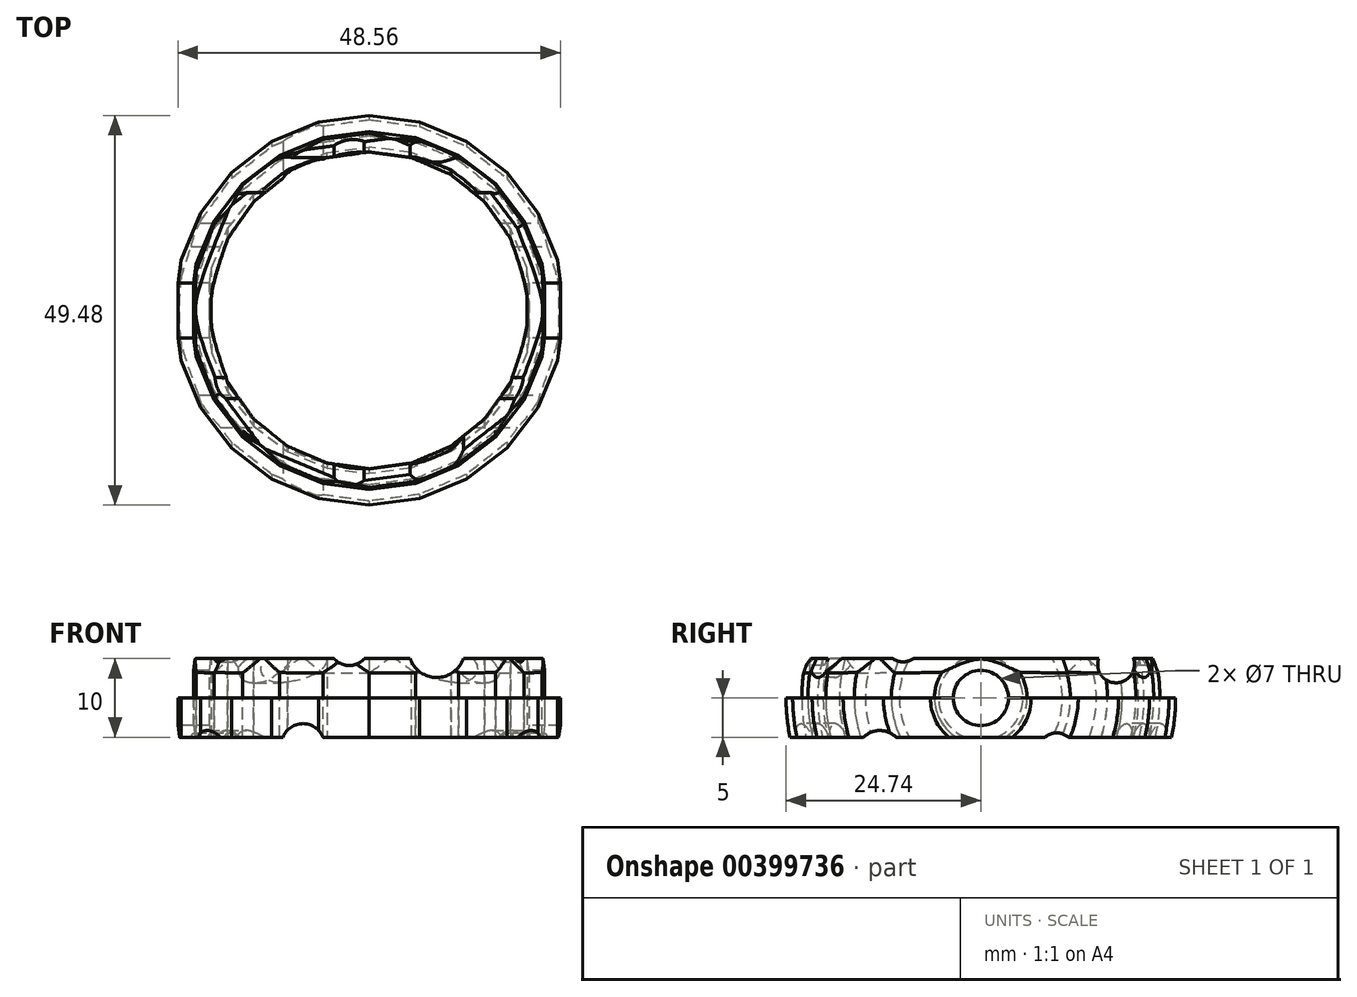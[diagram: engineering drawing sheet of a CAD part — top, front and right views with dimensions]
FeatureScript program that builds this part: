
annotation { "Feature Type Name" : "Feature", "Feature Type Description" : "" }
export const myFeature = defineFeature(function(context is Context, id is Id, definition is map)
    precondition{}
    {
        {
            var Q0;
            Q0=qCreatedBy(makeId("Top.planeOp"),FACE);
            var sketch = newSketch(context, id + "F0", { "sketchPlane" : qUnion([Q0])});
            skLineSegment(sketch, "E0", {"start": v(-24.74, 0) * mm, "end": v(24.74, 0) * mm});
            skLineSegment(sketch, "E1", {"start": v(-24.74, 0) * mm, "end": v(-22.74, 0) * mm});
            skLineSegment(sketch, "E2", {"start": v(24.74, 0) * mm, "end": v(22.74, 0) * mm});
            skLineSegment(sketch, "E3", {"start": v(0, 0) * mm, "end": v(-21.43, -12.37) * mm});
            skLineSegment(sketch, "E4", {"start": v(0, 0) * mm, "end": v(-23.9, -6.4) * mm});
            skLineSegment(sketch, "E5", {"start": v(-23.9, -6.4) * mm, "end": v(0, 0) * mm});
            skLineSegment(sketch, "E6", {"start": v(0, 0) * mm, "end": v(-17.5, -17.5) * mm});
            skLineSegment(sketch, "E7", {"start": v(-17.5, -17.5) * mm, "end": v(0, 0) * mm});
            skLineSegment(sketch, "E8", {"start": v(0, 0) * mm, "end": v(12.37, -21.43) * mm});
            skLineSegment(sketch, "E9", {"start": v(12.37, -21.43) * mm, "end": v(0, 0) * mm});
            skLineSegment(sketch, "E10", {"start": v(0, 0) * mm, "end": v(17.5, -17.5) * mm});
            skLineSegment(sketch, "E11", {"start": v(17.5, -17.5) * mm, "end": v(0, 0) * mm});
            skLineSegment(sketch, "E12", {"start": v(0, 0) * mm, "end": v(21.43, -12.37) * mm});
            skLineSegment(sketch, "E13", {"start": v(0, 0) * mm, "end": v(-12.37, -21.43) * mm});
            skLineSegment(sketch, "E14", {"start": v(-12.37, -21.43) * mm, "end": v(0, 0) * mm});
            skLineSegment(sketch, "E15", {"start": v(0, 0) * mm, "end": v(-6.4, -23.9) * mm});
            skLineSegment(sketch, "E16", {"start": v(0, 0) * mm, "end": v(6.4, -23.9) * mm});
            skLineSegment(sketch, "E17", {"start": v(0, 0) * mm, "end": v(23.9, -6.4) * mm});
            skLineSegment(sketch, "E18", {"start": v(0, 0) * mm, "end": v(0, -24.74) * mm});
            skSolve(sketch);
        }
        {
            var Q0;
            Q0=qCreatedBy(makeId("Top.planeOp"),FACE);
            var sketch = newSketch(context, id + "F1", { "sketchPlane" : qUnion([Q0])});
            skLineSegment(sketch, "E19", {"start": v(-24.74, 0) * mm, "end": v(-23.9, -6.4) * mm});
            skLineSegment(sketch, "E20", {"start": v(-23.9, -6.4) * mm, "end": v(-21.43, -12.37) * mm});
            skLineSegment(sketch, "E21", {"start": v(-21.43, -12.37) * mm, "end": v(-17.5, -17.5) * mm});
            skLineSegment(sketch, "E22", {"start": v(-17.5, -17.5) * mm, "end": v(-12.37, -21.43) * mm});
            skLineSegment(sketch, "E23", {"start": v(-12.37, -21.43) * mm, "end": v(-6.4, -23.9) * mm});
            skLineSegment(sketch, "E24", {"start": v(-6.4, -23.9) * mm, "end": v(0, -24.74) * mm});
            skLineSegment(sketch, "E25", {"start": v(0, -24.74) * mm, "end": v(6.4, -23.9) * mm});
            skLineSegment(sketch, "E26", {"start": v(6.4, -23.9) * mm, "end": v(12.37, -21.43) * mm});
            skLineSegment(sketch, "E27", {"start": v(12.37, -21.43) * mm, "end": v(17.5, -17.5) * mm});
            skLineSegment(sketch, "E28", {"start": v(17.5, -17.5) * mm, "end": v(21.43, -12.37) * mm});
            skLineSegment(sketch, "E29", {"start": v(21.43, -12.37) * mm, "end": v(23.9, -6.4) * mm});
            skLineSegment(sketch, "E30", {"start": v(23.9, -6.4) * mm, "end": v(24.74, 0) * mm});
            skLineSegment(sketch, "E31", {"start": v(-22.74, 0) * mm, "end": v(-21.97, -5.89) * mm});
            skLineSegment(sketch, "E32", {"start": v(-21.97, -5.89) * mm, "end": v(-19.7, -11.37) * mm});
            skLineSegment(sketch, "E33", {"start": v(-19.7, -11.37) * mm, "end": v(-16.08, -16.08) * mm});
            skLineSegment(sketch, "E34", {"start": v(-16.08, -16.08) * mm, "end": v(-11.37, -19.7) * mm});
            skLineSegment(sketch, "E35", {"start": v(-11.37, -19.7) * mm, "end": v(-5.89, -21.97) * mm});
            skLineSegment(sketch, "E36", {"start": v(-5.89, -21.97) * mm, "end": v(0, -22.74) * mm});
            skLineSegment(sketch, "E37", {"start": v(0, -22.74) * mm, "end": v(5.89, -21.97) * mm});
            skLineSegment(sketch, "E38", {"start": v(5.89, -21.97) * mm, "end": v(11.37, -19.7) * mm});
            skLineSegment(sketch, "E39", {"start": v(11.37, -19.7) * mm, "end": v(16.08, -16.08) * mm});
            skLineSegment(sketch, "E40", {"start": v(16.08, -16.08) * mm, "end": v(19.7, -11.37) * mm});
            skLineSegment(sketch, "E41", {"start": v(19.7, -11.37) * mm, "end": v(21.97, -5.89) * mm});
            skLineSegment(sketch, "E42", {"start": v(21.97, -5.89) * mm, "end": v(22.74, 0) * mm});
            skLineSegment(sketch, "E43", {"start": v(-24.74, 0) * mm, "end": v(-22.74, 0) * mm});
            skLineSegment(sketch, "E44", {"start": v(22.74, 0) * mm, "end": v(24.74, 0) * mm});
            skSolve(sketch);
        }
        {
            var Q0;
            Q0 = qSketchRegion(id + "F1", true);
            var Q1;
            Q1=sQuery(id+"F0.wireOp",EDGE,"E0");
            revolve(context, id + "F2", {"entities" : qUnion([Q0]), "axis" : qUnion([Q1]), "revolveType" : RevolveType.FULL});
        }
        {
            var Q0;
            Q0=qCreatedBy(makeId("Top.planeOp"),FACE);
            var sketch = newSketch(context, id + "F3", { "sketchPlane" : qUnion([Q0])});
            skLineSegment(sketch, "E45.bottom", {"start": v(-24.99, 25) * mm, "end": v(24.99, 25) * mm});
            skLineSegment(sketch, "E45.top", {"start": v(-24.99, -25) * mm, "end": v(24.99, -25) * mm});
            skLineSegment(sketch, "E45.left", {"start": v(-24.99, 25) * mm, "end": v(-24.99, -25) * mm});
            skLineSegment(sketch, "E45.right", {"start": v(24.99, 25) * mm, "end": v(24.99, -25) * mm});
            skPoint(sketch, "E45.middle", {"position": v(0, 0) * mm});
            skSolve(sketch);
        }
        {
            var Q0;
            Q0 = qSketchRegion(id + "F3", true);
            extrude(context, id + "F4", {"entities" : qUnion([Q0]), "operationType" : NewBodyOperationType.REMOVE, "depth" : 25 * mm});
        }
        {
            var Q0;
            Q0=qCreatedBy(makeId("Top.planeOp"),FACE);
            var sketch = newSketch(context, id + "F5", { "sketchPlane" : qUnion([Q0])});
            skLineSegment(sketch, "E46", {"start": v(-22.74, 0) * mm, "end": v(-21.97, -5.89) * mm});
            skLineSegment(sketch, "E47", {"start": v(-21.97, -5.89) * mm, "end": v(-19.7, -11.37) * mm});
            skLineSegment(sketch, "E48", {"start": v(-19.7, -11.37) * mm, "end": v(-16.08, -16.08) * mm});
            skLineSegment(sketch, "E49", {"start": v(-16.08, -16.08) * mm, "end": v(-11.37, -19.7) * mm});
            skLineSegment(sketch, "E50", {"start": v(-11.37, -19.7) * mm, "end": v(-5.89, -21.97) * mm});
            skLineSegment(sketch, "E51", {"start": v(-5.89, -21.97) * mm, "end": v(0, -22.74) * mm});
            skLineSegment(sketch, "E52", {"start": v(0, -22.74) * mm, "end": v(5.89, -21.97) * mm});
            skLineSegment(sketch, "E53", {"start": v(5.89, -21.97) * mm, "end": v(11.37, -19.7) * mm});
            skLineSegment(sketch, "E54", {"start": v(11.37, -19.7) * mm, "end": v(16.08, -16.08) * mm});
            skLineSegment(sketch, "E55", {"start": v(16.08, -16.08) * mm, "end": v(19.7, -11.37) * mm});
            skLineSegment(sketch, "E56", {"start": v(19.7, -11.37) * mm, "end": v(21.97, -5.89) * mm});
            skLineSegment(sketch, "E57", {"start": v(21.97, -5.89) * mm, "end": v(22.74, 0) * mm});
            skLineSegment(sketch, "E58", {"start": v(20.74, 0) * mm, "end": v(20.03, -5.37) * mm});
            skLineSegment(sketch, "E59", {"start": v(20.03, -5.37) * mm, "end": v(17.96, -10.37) * mm});
            skLineSegment(sketch, "E60", {"start": v(17.96, -10.37) * mm, "end": v(14.67, -14.67) * mm});
            skLineSegment(sketch, "E61", {"start": v(14.67, -14.67) * mm, "end": v(10.37, -17.96) * mm});
            skLineSegment(sketch, "E62", {"start": v(10.37, -17.96) * mm, "end": v(5.37, -20.03) * mm});
            skLineSegment(sketch, "E63", {"start": v(5.37, -20.03) * mm, "end": v(0, -20.74) * mm});
            skLineSegment(sketch, "E64", {"start": v(0, -20.74) * mm, "end": v(-5.37, -20.03) * mm});
            skLineSegment(sketch, "E65", {"start": v(-5.37, -20.03) * mm, "end": v(-10.37, -17.96) * mm});
            skLineSegment(sketch, "E66", {"start": v(-10.37, -17.96) * mm, "end": v(-14.67, -14.67) * mm});
            skLineSegment(sketch, "E67", {"start": v(-14.67, -14.67) * mm, "end": v(-17.96, -10.37) * mm});
            skLineSegment(sketch, "E68", {"start": v(-17.96, -10.37) * mm, "end": v(-20.03, -5.37) * mm});
            skLineSegment(sketch, "E69", {"start": v(-20.03, -5.37) * mm, "end": v(-20.74, 0) * mm});
            skLineSegment(sketch, "E70", {"start": v(-20.74, 0) * mm, "end": v(-22.74, 0) * mm});
            skLineSegment(sketch, "E71", {"start": v(20.74, 0) * mm, "end": v(22.74, 0) * mm});
            skSolve(sketch);
        }
        {
            var Q0;
            Q0 = qSketchRegion(id + "F5", true);
            var Q1;
            Q1=sQuery(id+"F0.wireOp",EDGE,"E0");
            revolve(context, id + "F6", {"entities" : qUnion([Q0]), "axis" : qUnion([Q1]), "revolveType" : RevolveType.FULL, "oppositeDirection" : true});
        }
        {
            var Q0;
            Q0=qCreatedBy(makeId("Top.planeOp"),FACE);
            var sketch = newSketch(context, id + "F7", { "sketchPlane" : qUnion([Q0])});
            skLineSegment(sketch, "E72.bottom", {"start": v(-27.5, 27.5) * mm, "end": v(27.5, 27.5) * mm});
            skLineSegment(sketch, "E72.top", {"start": v(-27.5, -27.5) * mm, "end": v(27.5, -27.5) * mm});
            skLineSegment(sketch, "E72.left", {"start": v(-27.5, 27.5) * mm, "end": v(-27.5, -27.5) * mm});
            skLineSegment(sketch, "E72.right", {"start": v(27.5, 27.5) * mm, "end": v(27.5, -27.5) * mm});
            skPoint(sketch, "E72.middle", {"position": v(0, 0) * mm});
            skSolve(sketch);
        }
        {
            var Q0;
            Q0 = qSketchRegion(id + "F7", true);
            extrude(context, id + "F8", {"entities" : qUnion([Q0]), "operationType" : NewBodyOperationType.REMOVE, "depth" : 25 * mm, "hasSecondDirection" : true, "secondDirectionOppositeDirection" : false, "secondDirectionDepth" : 5 * mm});
        }
        {
            var Q0;
            Q0=qCreatedBy(makeId("Top.planeOp"),FACE);
            var sketch = newSketch(context, id + "F9", { "sketchPlane" : qUnion([Q0])});
            skLineSegment(sketch, "E73.bottom", {"start": v(-30, 30) * mm, "end": v(30, 30) * mm});
            skLineSegment(sketch, "E73.top", {"start": v(-30, -30) * mm, "end": v(30, -30) * mm});
            skLineSegment(sketch, "E73.left", {"start": v(-30, 30) * mm, "end": v(-30, -30) * mm});
            skLineSegment(sketch, "E73.right", {"start": v(30, 30) * mm, "end": v(30, -30) * mm});
            skPoint(sketch, "E73.middle", {"position": v(0, 0) * mm});
            skSolve(sketch);
        }
        {
            var Q0;
            Q0 = qSketchRegion(id + "F9", true);
            extrude(context, id + "F10", {"entities" : qUnion([Q0]), "operationType" : NewBodyOperationType.REMOVE, "oppositeDirection" : true, "depth" : 25 * mm, "hasSecondDirection" : true, "secondDirectionOppositeDirection" : true, "secondDirectionDepth" : 5 * mm});
        }
        {
            var Q0;
            Q0=qCreatedBy(makeId("Right.planeOp"),FACE);
            var sketch = newSketch(context, id + "F11", { "sketchPlane" : qUnion([Q0])});
            skCircle(sketch, "E74", {"center": v(0, 0) * mm, "radius": 3.5 * mm});
            skSolve(sketch);
        }
        {
            var Q0;
            Q0 = qSketchRegion(id + "F11", true);
            extrude(context, id + "F12", {"entities" : qUnion([Q0]), "operationType" : NewBodyOperationType.REMOVE, "depth" : 25 * mm, "hasSecondDirection" : true, "secondDirectionOppositeDirection" : true, "secondDirectionDepth" : 25 * mm});
        }
        {
            var Q0;
            Q0=makeQuery(id+"F8.boolean.opBoolean","INTERSECT",EDGE,{"disambiguationData":[OD(0.0)],"derivedFrom":[makeQuery(id+"F6.opRevolve","SWEPT_FACE",FACE,{"disambiguationData":[OSD([sQuery(id+"F5.wireOp",EDGE,"E48")])]}),makeQuery(id+"F8.opExtrude","CAP_FACE",FACE,{"disambiguationData":[OSD([sQuery(id+"F7.wireOp",EDGE,"E72.bottom"),sQuery(id+"F7.wireOp",EDGE,"E72.top"),sQuery(id+"F7.wireOp",EDGE,"E72.left"),sQuery(id+"F7.wireOp",EDGE,"E72.right")])],"isStart":true})]});
            var Q1;
            Q1=makeQuery(id+"F8.boolean.opBoolean","INTERSECT",EDGE,{"disambiguationData":[OD(0.0)],"derivedFrom":[makeQuery(id+"F6.opRevolve","SWEPT_FACE",FACE,{"disambiguationData":[OSD([sQuery(id+"F5.wireOp",EDGE,"E50")])]}),makeQuery(id+"F8.opExtrude","CAP_FACE",FACE,{"disambiguationData":[OSD([sQuery(id+"F7.wireOp",EDGE,"E72.bottom"),sQuery(id+"F7.wireOp",EDGE,"E72.top"),sQuery(id+"F7.wireOp",EDGE,"E72.left"),sQuery(id+"F7.wireOp",EDGE,"E72.right")])],"isStart":true})]});
            var Q2;
            Q2=makeQuery(id+"F8.boolean.opBoolean","INTERSECT",EDGE,{"disambiguationData":[OD(0.0)],"derivedFrom":[makeQuery(id+"F6.opRevolve","SWEPT_FACE",FACE,{"disambiguationData":[OSD([sQuery(id+"F5.wireOp",EDGE,"E52")])]}),makeQuery(id+"F8.opExtrude","CAP_FACE",FACE,{"disambiguationData":[OSD([sQuery(id+"F7.wireOp",EDGE,"E72.bottom"),sQuery(id+"F7.wireOp",EDGE,"E72.top"),sQuery(id+"F7.wireOp",EDGE,"E72.left"),sQuery(id+"F7.wireOp",EDGE,"E72.right")])],"isStart":true})]});
            var Q3;
            Q3=makeQuery(id+"F8.boolean.opBoolean","INTERSECT",EDGE,{"disambiguationData":[OD(0.0)],"derivedFrom":[makeQuery(id+"F6.opRevolve","SWEPT_FACE",FACE,{"disambiguationData":[OSD([sQuery(id+"F5.wireOp",EDGE,"E54")])]}),makeQuery(id+"F8.opExtrude","CAP_FACE",FACE,{"disambiguationData":[OSD([sQuery(id+"F7.wireOp",EDGE,"E72.bottom"),sQuery(id+"F7.wireOp",EDGE,"E72.top"),sQuery(id+"F7.wireOp",EDGE,"E72.left"),sQuery(id+"F7.wireOp",EDGE,"E72.right")])],"isStart":true})]});
            var Q4;
            Q4=makeQuery(id+"F8.boolean.opBoolean","INTERSECT",EDGE,{"disambiguationData":[OD(1.0)],"derivedFrom":[makeQuery(id+"F6.opRevolve","SWEPT_FACE",FACE,{"disambiguationData":[OSD([sQuery(id+"F5.wireOp",EDGE,"E55")])]}),makeQuery(id+"F8.opExtrude","CAP_FACE",FACE,{"disambiguationData":[OSD([sQuery(id+"F7.wireOp",EDGE,"E72.bottom"),sQuery(id+"F7.wireOp",EDGE,"E72.top"),sQuery(id+"F7.wireOp",EDGE,"E72.left"),sQuery(id+"F7.wireOp",EDGE,"E72.right")])],"isStart":true})]});
            var Q5;
            Q5=makeQuery(id+"F8.boolean.opBoolean","INTERSECT",EDGE,{"disambiguationData":[OD(1.0)],"derivedFrom":[makeQuery(id+"F6.opRevolve","SWEPT_FACE",FACE,{"disambiguationData":[OSD([sQuery(id+"F5.wireOp",EDGE,"E53")])]}),makeQuery(id+"F8.opExtrude","CAP_FACE",FACE,{"disambiguationData":[OSD([sQuery(id+"F7.wireOp",EDGE,"E72.bottom"),sQuery(id+"F7.wireOp",EDGE,"E72.top"),sQuery(id+"F7.wireOp",EDGE,"E72.left"),sQuery(id+"F7.wireOp",EDGE,"E72.right")])],"isStart":true})]});
            var Q6;
            Q6=makeQuery(id+"F8.boolean.opBoolean","INTERSECT",EDGE,{"disambiguationData":[OD(1.0)],"derivedFrom":[makeQuery(id+"F6.opRevolve","SWEPT_FACE",FACE,{"disambiguationData":[OSD([sQuery(id+"F5.wireOp",EDGE,"E51")])]}),makeQuery(id+"F8.opExtrude","CAP_FACE",FACE,{"disambiguationData":[OSD([sQuery(id+"F7.wireOp",EDGE,"E72.bottom"),sQuery(id+"F7.wireOp",EDGE,"E72.top"),sQuery(id+"F7.wireOp",EDGE,"E72.left"),sQuery(id+"F7.wireOp",EDGE,"E72.right")])],"isStart":true})]});
            var Q7;
            Q7=makeQuery(id+"F8.boolean.opBoolean","INTERSECT",EDGE,{"disambiguationData":[OD(1.0)],"derivedFrom":[makeQuery(id+"F6.opRevolve","SWEPT_FACE",FACE,{"disambiguationData":[OSD([sQuery(id+"F5.wireOp",EDGE,"E49")])]}),makeQuery(id+"F8.opExtrude","CAP_FACE",FACE,{"disambiguationData":[OSD([sQuery(id+"F7.wireOp",EDGE,"E72.bottom"),sQuery(id+"F7.wireOp",EDGE,"E72.top"),sQuery(id+"F7.wireOp",EDGE,"E72.left"),sQuery(id+"F7.wireOp",EDGE,"E72.right")])],"isStart":true})]});
            var Q8;
            Q8=makeQuery(id+"F8.boolean.opBoolean","INTERSECT",EDGE,{"disambiguationData":[OD(0.0)],"derivedFrom":[makeQuery(id+"F6.opRevolve","SWEPT_FACE",FACE,{"disambiguationData":[OSD([sQuery(id+"F5.wireOp",EDGE,"E56")])]}),makeQuery(id+"F8.opExtrude","CAP_FACE",FACE,{"disambiguationData":[OSD([sQuery(id+"F7.wireOp",EDGE,"E72.bottom"),sQuery(id+"F7.wireOp",EDGE,"E72.top"),sQuery(id+"F7.wireOp",EDGE,"E72.left"),sQuery(id+"F7.wireOp",EDGE,"E72.right")])],"isStart":true})]});
            var Q9;
            Q9=makeQuery(id+"F8.boolean.opBoolean","INTERSECT",EDGE,{"disambiguationData":[OD(1.0)],"derivedFrom":[makeQuery(id+"F6.opRevolve","SWEPT_FACE",FACE,{"disambiguationData":[OSD([sQuery(id+"F5.wireOp",EDGE,"E47")])]}),makeQuery(id+"F8.opExtrude","CAP_FACE",FACE,{"disambiguationData":[OSD([sQuery(id+"F7.wireOp",EDGE,"E72.bottom"),sQuery(id+"F7.wireOp",EDGE,"E72.top"),sQuery(id+"F7.wireOp",EDGE,"E72.left"),sQuery(id+"F7.wireOp",EDGE,"E72.right")])],"isStart":true})]});
            chamfer(context, id + "F13", {"entities" : qUnion([Q0, Q1, Q2, Q3, Q4, Q5, Q6, Q7, Q8, Q9]), "chamferType" : ChamferType.OFFSET_ANGLE, "width" : 0.5 * mm, "oppositeDirection" : false, "angle" : 60 * degree, "tangentPropagation" : true});
        }
        {
            var Q0;
            Q0=qCreatedBy(makeId("Top.planeOp"),FACE);
            var sketch = newSketch(context, id + "F14", { "sketchPlane" : qUnion([Q0])});
            skCircle(sketch, "E75", {"center": v(8.17, -10.22) * mm, "radius": 3.72 * mm});
            skCircle(sketch, "E76", {"center": v(-7.31, -7.48) * mm, "radius": 3.44 * mm});
            skCircle(sketch, "E77", {"center": v(-12.03, 6.48) * mm, "radius": 2.57 * mm});
            skCircle(sketch, "E78", {"center": v(-2.27, 10.44) * mm, "radius": 4.06 * mm});
            skCircle(sketch, "E79", {"center": v(8.4, 2.88) * mm, "radius": 2.25 * mm});
            skCircle(sketch, "E80", {"center": v(12.25, 9.37) * mm, "radius": 2.73 * mm});
            skSolve(sketch);
        }
        {
            var Q0;
            Q0 = qSketchRegion(id + "F14", true);
            extrude(context, id + "F15", {"entities" : qUnion([Q0]), "operationType" : NewBodyOperationType.REMOVE, "depth" : 25 * mm, "hasSecondDirection" : true, "secondDirectionOppositeDirection" : true, "secondDirectionDepth" : 25 * mm});
        }
        {
            var Q0;
            Q0=qCreatedBy(makeId("Right.planeOp"),FACE);
            var sketch = newSketch(context, id + "F16", { "sketchPlane" : qUnion([Q0])});
            skCircle(sketch, "E81", {"center": v(-12.82, -7.05) * mm, "radius": 2.9 * mm});
            skCircle(sketch, "E82", {"center": v(-4.05, -8.29) * mm, "radius": 1.93 * mm});
            skCircle(sketch, "E83", {"center": v(0, -14.27) * mm, "radius": 2.37 * mm});
            skCircle(sketch, "E84", {"center": v(9.62, -6.67) * mm, "radius": 2.24 * mm});
            skCircle(sketch, "E85", {"center": v(4.9, 10.82) * mm, "radius": 2.26 * mm});
            skCircle(sketch, "E86", {"center": v(17.17, 4.25) * mm, "radius": 2.33 * mm});
            skCircle(sketch, "E87", {"center": v(-9.87, 7.03) * mm, "radius": 2.43 * mm});
            skSolve(sketch);
        }
        {
            var Q0;
            Q0 = qSketchRegion(id + "F16", true);
            extrude(context, id + "F17", {"entities" : qUnion([Q0]), "operationType" : NewBodyOperationType.REMOVE, "oppositeDirection" : true, "depth" : 25 * mm, "hasSecondDirection" : true, "secondDirectionOppositeDirection" : false, "secondDirectionDepth" : 25 * mm});
        }
        {
            var Q0;
            Q0=qCreatedBy(makeId("Front.planeOp"),FACE);
            var sketch = newSketch(context, id + "F18", { "sketchPlane" : qUnion([Q0])});
            skCircle(sketch, "E88", {"center": v(-8.4, -6) * mm, "radius": 2.73 * mm});
            skCircle(sketch, "E89", {"center": v(-2.71, -12.1) * mm, "radius": 3.38 * mm});
            skCircle(sketch, "E90", {"center": v(7.3, -8.97) * mm, "radius": 1.45 * mm});
            skCircle(sketch, "E91", {"center": v(8.58, 6.17) * mm, "radius": 3.57 * mm});
            skCircle(sketch, "E92", {"center": v(-2.54, 6.65) * mm, "radius": 2.53 * mm});
            skCircle(sketch, "E93", {"center": v(-10.55, 10.22) * mm, "radius": 2.94 * mm});
            skSolve(sketch);
        }
        {
            var Q0;
            Q0 = qSketchRegion(id + "F18", true);
            extrude(context, id + "F19", {"entities" : qUnion([Q0]), "operationType" : NewBodyOperationType.REMOVE, "oppositeDirection" : true, "depth" : 25 * mm, "hasSecondDirection" : true, "secondDirectionOppositeDirection" : false, "secondDirectionDepth" : 25 * mm});
        }
    });
